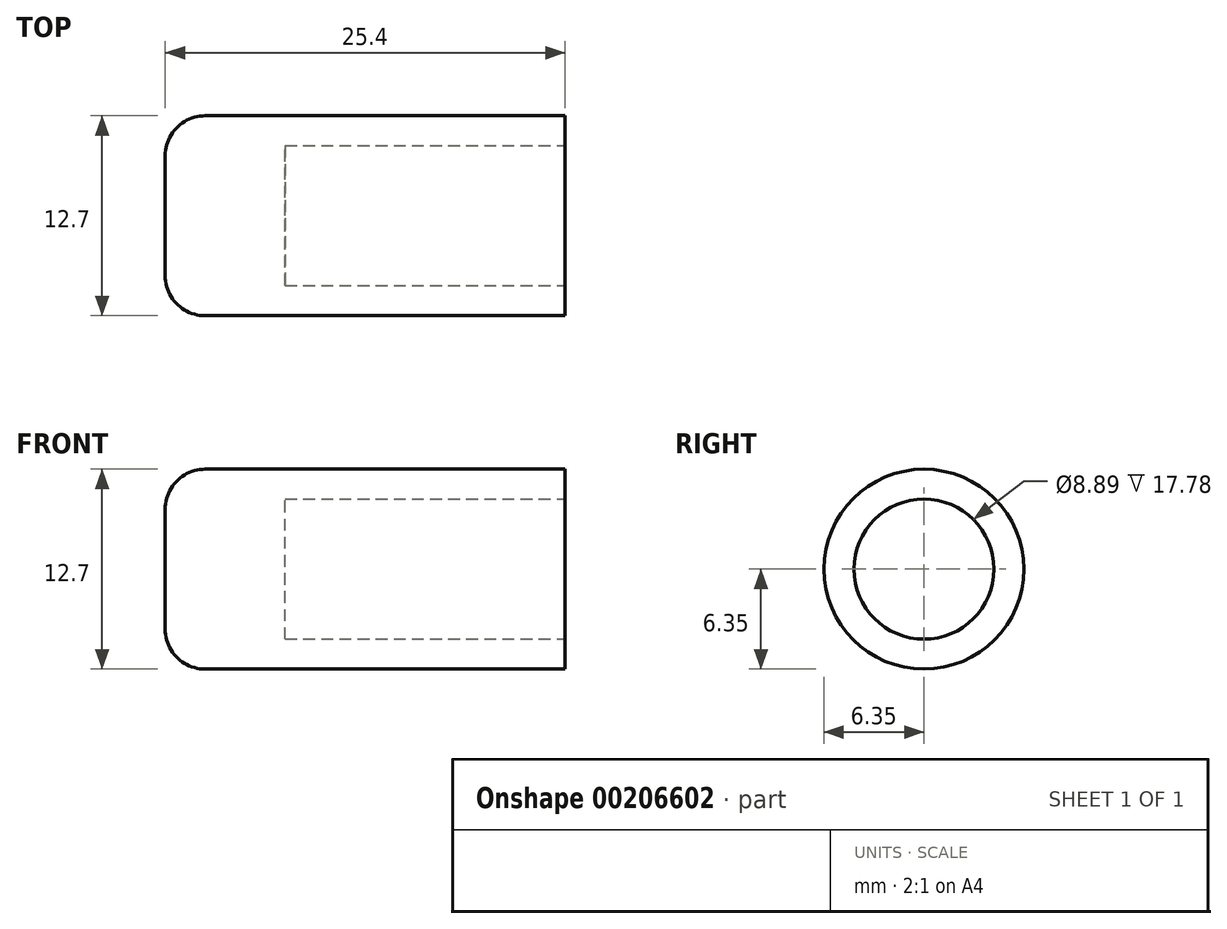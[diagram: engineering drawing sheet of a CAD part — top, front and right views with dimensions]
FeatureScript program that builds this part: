
annotation { "Feature Type Name" : "Feature", "Feature Type Description" : "" }
export const myFeature = defineFeature(function(context is Context, id is Id, definition is map)
    precondition{}
    {
        {
            var Q0;
            Q0=qCreatedBy(makeId("Right.planeOp"),FACE);
            var sketch = newSketch(context, id + "F0", { "sketchPlane" : qUnion([Q0])});
            skCircle(sketch, "E0", {"center": v(0, 0) * mm, "radius": 6.35 * mm});
            skSolve(sketch);
        }
        {
            var Q0;
            Q0=makeQuery(id+"F0.imprint","IMPRINT",FACE,{"disambiguationData":[TD([[makeQuery(id+"F0.imprint","IMPRINT",EDGE,{"derivedFrom":sQuery(id+"F0.wireOp",EDGE,"E0")}),1.0]])]});
            var Q1;
            Q1=sQuery(id+"F0.wireOp",EDGE,"E0");
            extrude(context, id + "F1", {"entities" : qUnion([Q0]), "surfaceEntities" : qUnion([Q1]), "depth" : 25.4 * mm});
        }
        {
            var Q0;
            Q0=makeQuery(id+"F1.opExtrude","CAP_FACE",FACE,{"disambiguationData":[OSD([sQuery(id+"F0.wireOp",EDGE,"E0")])],"isStart":false});
            var sketch = newSketch(context, id + "F2", { "sketchPlane" : qUnion([Q0])});
            skCircle(sketch, "E1", {"center": v(0, 0) * mm, "radius": 4.45 * mm});
            skSolve(sketch);
        }
        {
            var Q0;
            Q0=makeQuery(id+"F2.imprint","IMPRINT",FACE,{"disambiguationData":[TD([[makeQuery(id+"F2.imprint","IMPRINT",EDGE,{"derivedFrom":sQuery(id+"F2.wireOp",EDGE,"E1")}),1.0]])]});
            extrude(context, id + "F3", {"entities" : qUnion([Q0]), "operationType" : NewBodyOperationType.REMOVE, "oppositeDirection" : true, "depth" : 17.78 * mm});
        }
        {
            var Q0;
            Q0=makeQuery(id+"F1.opExtrude","CAP_EDGE",EDGE,{"disambiguationData":[OSD([sQuery(id+"F0.wireOp",EDGE,"E0")])],"isStart":true});
            fillet(context, id + "F4", {"entities" : qUnion([Q0]), "radius" : 2.54 * mm, "tangentPropagation" : true, "allowEdgeOverflow" : false});
        }
    });
